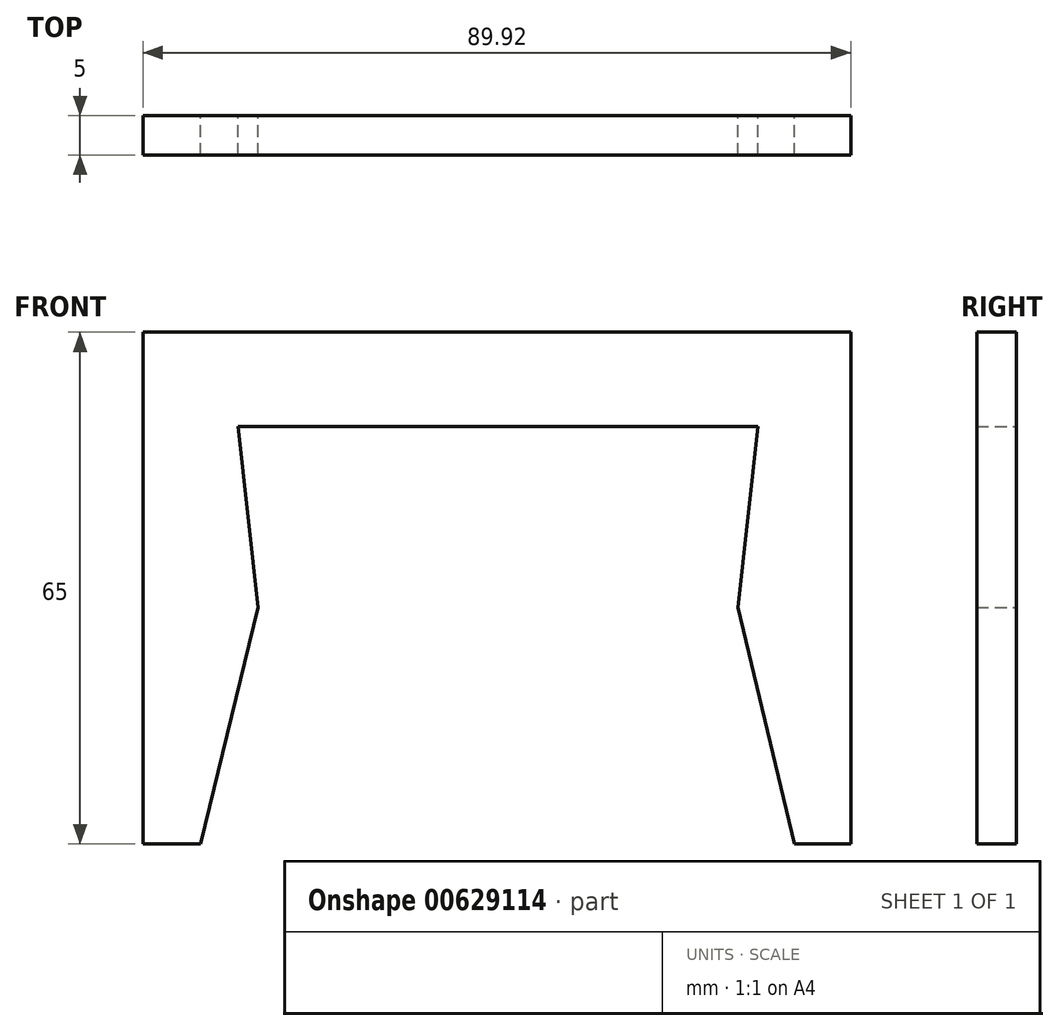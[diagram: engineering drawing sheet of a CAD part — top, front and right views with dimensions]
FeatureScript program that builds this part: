
annotation { "Feature Type Name" : "Feature", "Feature Type Description" : "" }
export const myFeature = defineFeature(function(context is Context, id is Id, definition is map)
    precondition{}
    {
        {
            var Q0;
            Q0=qCreatedBy(makeId("Front.planeOp"),FACE);
            var sketch = newSketch(context, id + "F0", { "sketchPlane" : qUnion([Q0])});
            skLineSegment(sketch, "E0", {"start": v(0, 46) * mm, "end": v(33, 46) * mm});
            skLineSegment(sketch, "E1", {"start": v(0, 46) * mm, "end": v(-33, 46) * mm});
            skLineSegment(sketch, "E2", {"start": v(0, 46) * mm, "end": v(0, 0) * mm});
            skLineSegment(sketch, "E3", {"start": v(-45.09, 58) * mm, "end": v(-45.09, -7) * mm});
            skLineSegment(sketch, "E4", {"start": v(44.83, 58) * mm, "end": v(44.83, -7) * mm});
            skLineSegment(sketch, "E5", {"start": v(-45.09, 58) * mm, "end": v(44.83, 58) * mm});
            skLineSegment(sketch, "E6", {"start": v(-33, 46) * mm, "end": v(-30.5, 23) * mm});
            skLineSegment(sketch, "E7", {"start": v(33, 46) * mm, "end": v(30.5, 23) * mm});
            skLineSegment(sketch, "E8", {"start": v(-30.5, 23) * mm, "end": v(-37.8, -7) * mm});
            skLineSegment(sketch, "E9", {"start": v(30.5, 23) * mm, "end": v(37.67, -7) * mm});
            skLineSegment(sketch, "E10", {"start": v(37.67, -7) * mm, "end": v(44.83, -7) * mm});
            skLineSegment(sketch, "E11", {"start": v(-45.09, -7) * mm, "end": v(-37.8, -7) * mm});
            skSolve(sketch);
        }
        {
            var Q0;
            Q0 = qSketchRegion(id + "F0", true);
            extrude(context, id + "F1", {"entities" : qUnion([Q0]), "depth" : 5 * mm, "offsetDistance" : 25 * mm});
        }
    });
